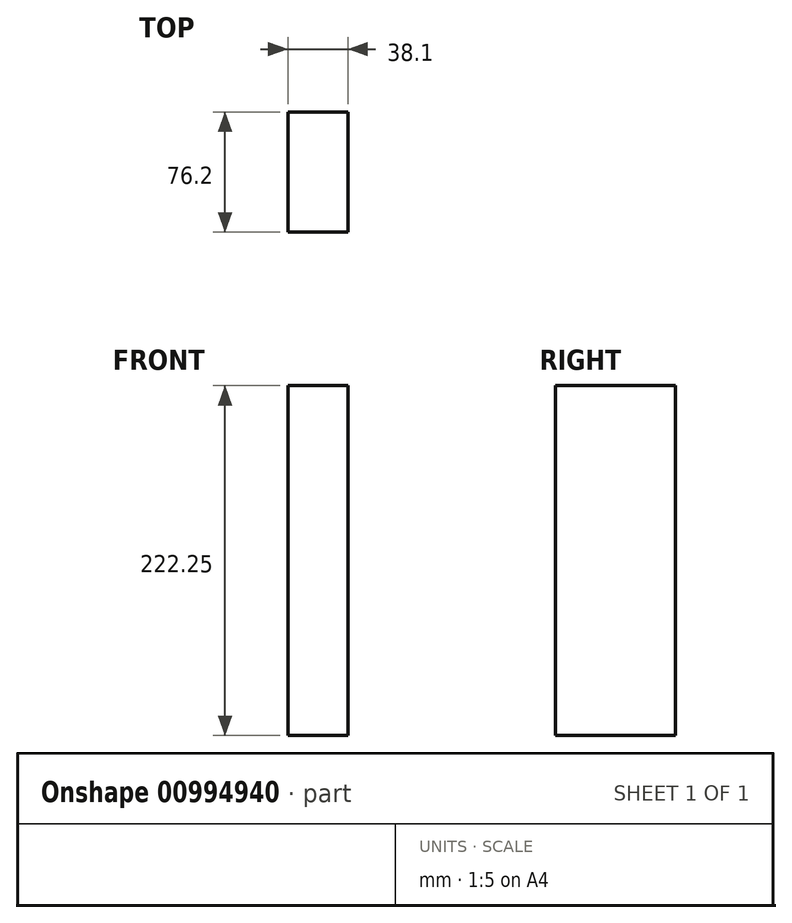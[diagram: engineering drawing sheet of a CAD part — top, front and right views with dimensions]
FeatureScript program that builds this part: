
annotation { "Feature Type Name" : "Feature", "Feature Type Description" : "" }
export const myFeature = defineFeature(function(context is Context, id is Id, definition is map)
    precondition{}
    {
        {
            var Q0;
            Q0=qCreatedBy(makeId("Front.planeOp"),FACE);
            var sketch = newSketch(context, id + "F0", { "sketchPlane" : qUnion([Q0])});
            skLineSegment(sketch, "E0.bottom", {"start": v(-19.05, 0) * mm, "end": v(19.05, 0) * mm});
            skLineSegment(sketch, "E0.top", {"start": v(-19.05, 222.25) * mm, "end": v(19.05, 222.25) * mm});
            skLineSegment(sketch, "E0.left", {"start": v(-19.05, 0) * mm, "end": v(-19.05, 222.25) * mm});
            skLineSegment(sketch, "E0.right", {"start": v(19.05, 0) * mm, "end": v(19.05, 222.25) * mm});
            skSolve(sketch);
        }
        {
            var Q0;
            Q0 = qSketchRegion(id + "F0", true);
            extrude(context, id + "F1", {"entities" : qUnion([Q0]), "oppositeDirection" : true, "depth" : 76.2 * mm, "offsetDistance" : 25.4 * mm});
        }
    });
